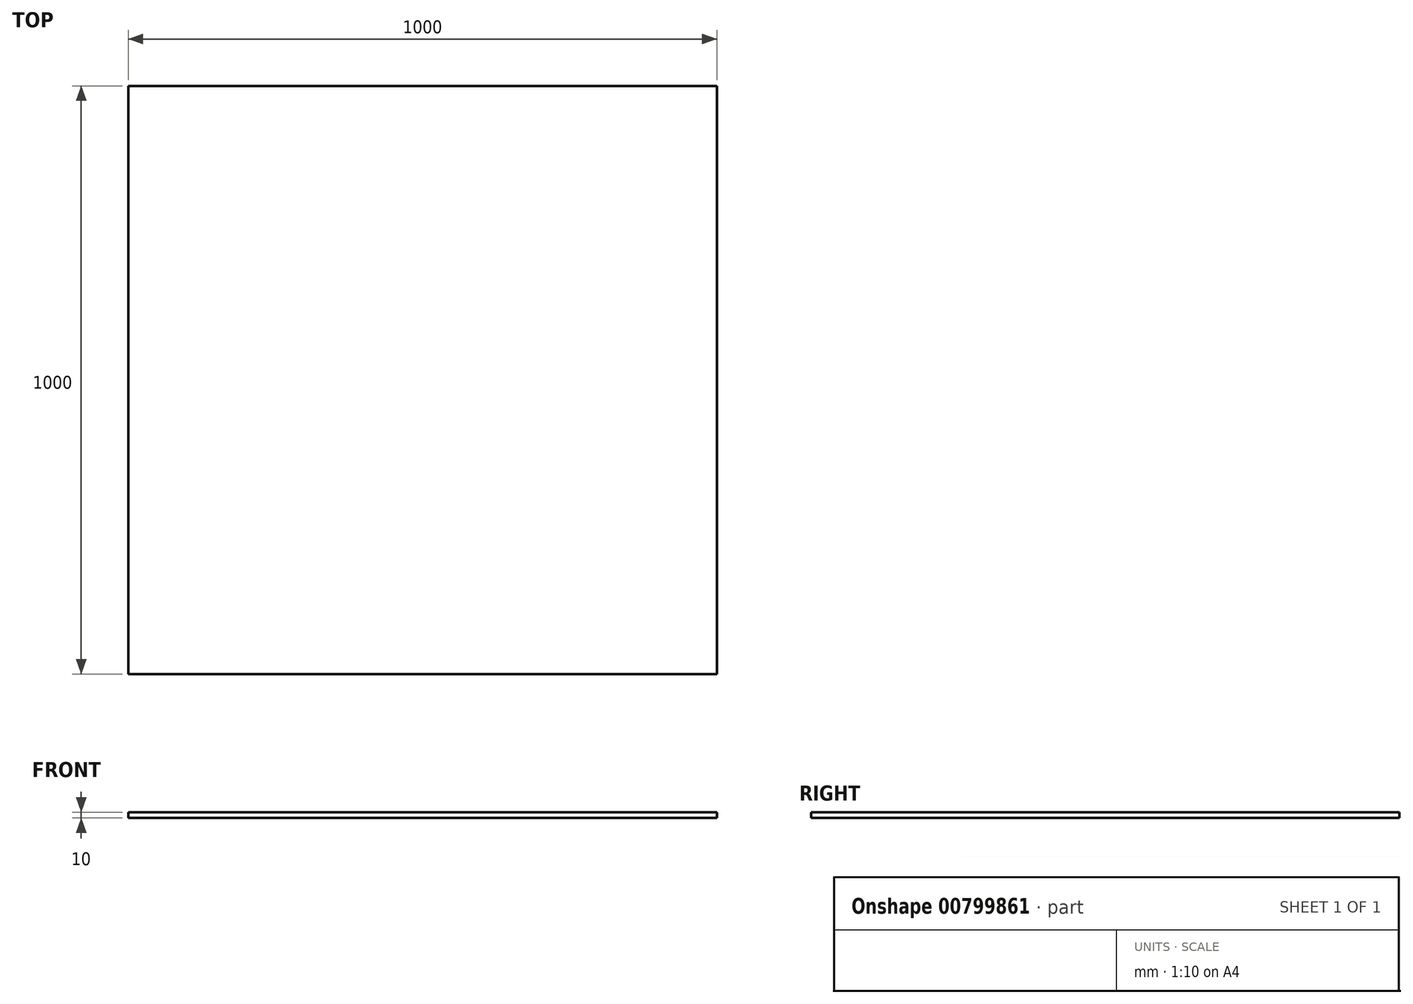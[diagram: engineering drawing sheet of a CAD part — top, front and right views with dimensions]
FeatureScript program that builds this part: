
annotation { "Feature Type Name" : "Feature", "Feature Type Description" : "" }
export const myFeature = defineFeature(function(context is Context, id is Id, definition is map)
    precondition{}
    {
        {
            var Q0;
            Q0=qCreatedBy(makeId("Top.planeOp"),FACE);
            var sketch = newSketch(context, id + "F0", { "sketchPlane" : qUnion([Q0])});
            skLineSegment(sketch, "E0.bottom", {"start": v(500, -500) * mm, "end": v(-500, -500) * mm});
            skLineSegment(sketch, "E0.top", {"start": v(500, 500) * mm, "end": v(-500, 500) * mm});
            skLineSegment(sketch, "E0.left", {"start": v(500, -500) * mm, "end": v(500, 500) * mm});
            skLineSegment(sketch, "E0.right", {"start": v(-500, -500) * mm, "end": v(-500, 500) * mm});
            skPoint(sketch, "E0.middle", {"position": v(0, 0) * mm});
            skSolve(sketch);
        }
        {
            var Q0;
            Q0=makeQuery(id+"F0.imprint","IMPRINT",FACE,{"disambiguationData":[TD([[makeQuery(id+"F0.imprint","IMPRINT",EDGE,{"derivedFrom":sQuery(id+"F0.wireOp",EDGE,"E0.bottom")}),-1.0]])]});
            extrude(context, id + "F1", {"entities" : qUnion([Q0]), "depth" : 10 * mm, "offsetDistance" : 25 * mm});
        }
    });
